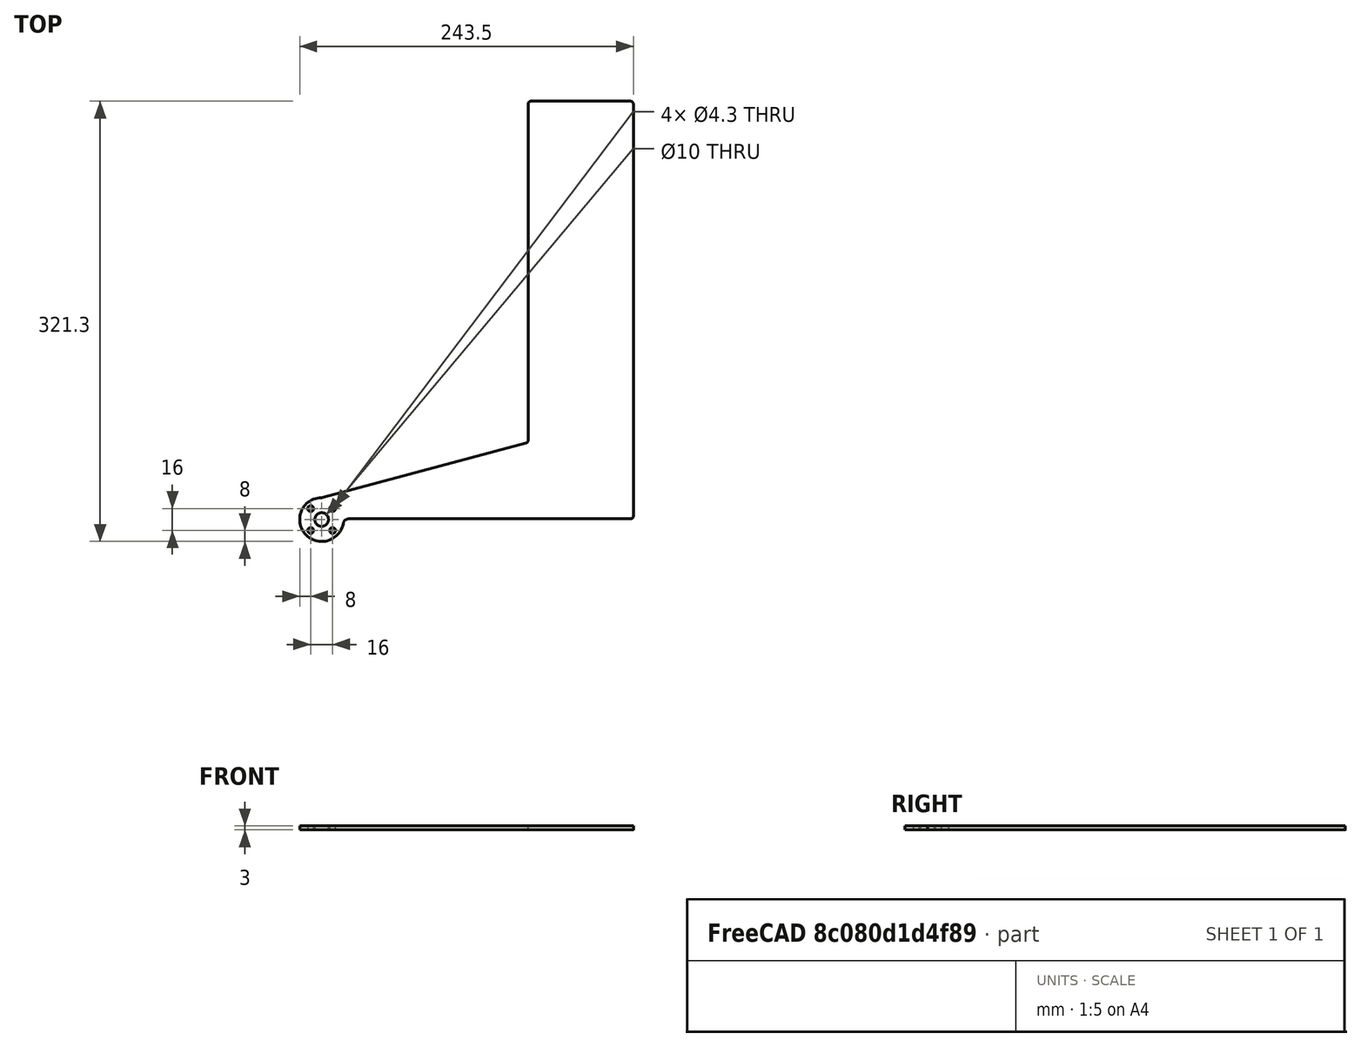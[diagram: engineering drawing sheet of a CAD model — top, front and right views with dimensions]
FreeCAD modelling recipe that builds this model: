
FCSTD DOCUMENT  (FreeCAD 0.20R29603 (Git))
Label: sleep_box_door
License: All rights reserved
LicenseURL: http://en.wikipedia.org/wiki/All_rights_reserved
objects: Sketcher::SketchObject×1, Spreadsheet::Sheet×1, PartDesign::Pad×1, PartDesign::Body×1, Part::Part2DObjectPython×1
note: 5 computed .brp shape members not serialized (recipe doc carries the construction recipe); baked Part::Feature solids carry a one-line shape summary decoded from their .brp

FEATURE [Sketcher::SketchObject] Sketch  label="DoorSketch"
  FullyConstrained = true
  MapMode = 5
  Support = -> [XY_Plane]
  expr: Constraints[11] = Spreadsheet.DoorFilletRadius
  expr: Constraints[1] = Spreadsheet.DoorHubDiameter
  expr: Constraints[25] = Spreadsheet.DoorToMazeFloorMargin
  expr: Constraints[30] = Spreadsheet.DoorHubFilletRadius
  expr: Constraints[35] = Spreadsheet.ServoSplineToMazeFloorDistance
  expr: Constraints[3] = Spreadsheet.DoorBottomLength
  expr: Constraints[53] = Spreadsheet.ServoHubMountThruHoleDiameter
  expr: Constraints[54] = Spreadsheet.ServoHubMountHoleSpacing
  expr: Constraints[56] = Spreadsheet.ServoHubCenterHoleDiameter
  expr: Constraints[5] = Spreadsheet.DoorHeight
  expr: Constraints[69] = Spreadsheet.DoorTopLength
  expr: Constraints[72] = Spreadsheet.DoorFilletRadius
  expr: Constraints[76] = Spreadsheet.DoorArmAngle
  sketch-geometry (32):
    g0: Circle CenterX=0 CenterY=0 CenterZ=0 NormalX=0 NormalY=0 NormalZ=1 AngleXU=0 Radius=16
    g1: LineSegment StartX=36.7 StartY=0.5 StartZ=0 EndX=225.5 EndY=0.5 EndZ=0
    g2: LineSegment StartX=227.5 StartY=2.5 StartZ=0 EndX=227.5 EndY=303.3 EndZ=0
    g3: LineSegment StartX=225.5 StartY=305.3 StartZ=0 EndX=152.7 EndY=305.3 EndZ=0
    g4: ArcOfCircle CenterX=225.5 CenterY=2.5 CenterZ=0 NormalX=0 NormalY=0 NormalZ=1 AngleXU=0 Radius=2 StartAngle=4.71239 EndAngle=6.28319
    g5: GeomPoint X=227.5 Y=0.5 Z=0
    g6: ArcOfCircle CenterX=225.5 CenterY=303.3 CenterZ=0 NormalX=0 NormalY=0 NormalZ=1 AngleXU=0 Radius=2 StartAngle=-1.8e-15 EndAngle=1.5708
    g7: GeomPoint X=227.5 Y=305.3 Z=0
    g8: LineSegment StartX=152.7 StartY=305.3 StartZ=0 EndX=36.7 EndY=0.5 EndZ=0
    g9: ArcOfCircle CenterX=152.7 CenterY=303.3 CenterZ=0 NormalX=0 NormalY=0 NormalZ=1 AngleXU=0 Radius=2 StartAngle=1.5708 EndAngle=3.14159
    g10: GeomPoint X=152.7 Y=305.3 Z=0
    g11: ArcOfCircle CenterX=0 CenterY=0 CenterZ=0 NormalX=0 NormalY=0 NormalZ=1 AngleXU=0 Radius=16 StartAngle=1.5708 EndAngle=6.10728
    g12: LineSegment StartX=36.7 StartY=0 StartZ=0 EndX=36.7 EndY=0.5 EndZ=0
    g13: LineSegment StartX=36.7 StartY=0.5 StartZ=0 EndX=19.6914 EndY=0.5 EndZ=0
    g14: ArcOfCircle CenterX=19.6914 CenterY=-3.5 CenterZ=0 NormalX=0 NormalY=0 NormalZ=1 AngleXU=0 Radius=4 StartAngle=1.5708 EndAngle=2.96569
    g15: ArcOfCircle CenterX=5e-16 CenterY=20 CenterZ=0 NormalX=0 NormalY=0 NormalZ=1 AngleXU=0 Radius=4 StartAngle=4.71239 EndAngle=4.97419
    g16: LineSegment StartX=-8 StartY=8 StartZ=0 EndX=8 EndY=8 EndZ=0
    g17: LineSegment StartX=8 StartY=8 StartZ=0 EndX=8 EndY=-8 EndZ=0
    g18: LineSegment StartX=8 StartY=-8 StartZ=0 EndX=-8 EndY=-8 EndZ=0
    g19: LineSegment StartX=-8 StartY=-8 StartZ=0 EndX=-8 EndY=8 EndZ=0
    g20: Circle CenterX=-8 CenterY=8 CenterZ=0 NormalX=0 NormalY=0 NormalZ=1 AngleXU=0 Radius=2.15
    g21: Circle CenterX=8 CenterY=8 CenterZ=0 NormalX=0 NormalY=0 NormalZ=1 AngleXU=0 Radius=2.15
    g22: Circle CenterX=-8 CenterY=-8 CenterZ=0 NormalX=0 NormalY=0 NormalZ=1 AngleXU=0 Radius=2.15
    g23: Circle CenterX=8 CenterY=-8 CenterZ=0 NormalX=0 NormalY=0 NormalZ=1 AngleXU=0 Radius=2.15
    g24: Circle CenterX=0 CenterY=0 CenterZ=0 NormalX=0 NormalY=0 NormalZ=1 AngleXU=0 Radius=5
    g25: LineSegment StartX=152.7 StartY=305.3 StartZ=0 EndX=152.7 EndY=0.5 EndZ=0
    g26: LineSegment StartX=36.7 StartY=0.5 StartZ=0 EndX=36.7 EndY=305.3 EndZ=0
    g27: LineSegment StartX=36.7 StartY=305.3 StartZ=0 EndX=152.7 EndY=305.3 EndZ=0
    g28: LineSegment StartX=1.03528 StartY=16.1363 StartZ=0 EndX=149.218 EndY=55.8416 EndZ=0
    g29: LineSegment StartX=150.7 StartY=303.3 StartZ=0 EndX=150.7 EndY=57.7735 EndZ=0
    g30: ArcOfCircle CenterX=148.7 CenterY=57.7735 CenterZ=0 NormalX=0 NormalY=0 NormalZ=1 AngleXU=0 Radius=2 StartAngle=4.97419 EndAngle=6.28319
    g31: LineSegment StartX=-2e-16 StartY=16 StartZ=0 EndX=152.7 EndY=16 EndZ=0
  constraints (77):
    c: Coincident(g0,g-1)
    c: Diameter(g0) = 32
    c: Horizontal(g1)
    c: DistanceX(g1,g5) = 190.8
    c: Vertical(g2)
    c: DistanceY(g5,g7) = 304.8
    c: Horizontal(g3)
    c: PointOnObject(g5,g1)
    c: PointOnObject(g5,g2)
    c: Tangent(g1,g4) = -1.5708
    c: Tangent(g2,g4) = -1.5708
    c: Radius(g4) = 2
    c: PointOnObject(g7,g3)
    c: PointOnObject(g7,g2)
    c: Tangent(g3,g6) = -1.5708
    c: Tangent(g2,g6) = -1.5708
    c: Equal(g4,g6)
    c: Coincident(g8,g10)
    c: Tangent(g3,g9) = -1.5708
    c: Equal(g6,g9)
    c: Coincident(g11,g0)
    c: PointOnObject(g11,g0)
    c: PointOnObject(g12,g-1)
    c: Vertical(g12)
    c: Coincident(g12,g1)
    c: DistanceY(g12,g12) = 0.5
    c: Coincident(g13,g1)
    c: Horizontal(g13)
    c: Tangent(g14,g13) = -1.5708
    c: Tangent(g14,g11) = 1.5708
    c: Radius(g14) = 4
    c: Tangent(g11,g15) = 1.5708
    c: Equal(g15,g14)
    c: PointOnObject(g11,g-2)
    c: Coincident(g8,g1)
    c: DistanceX(g11,g1) = 36.7
    c: Coincident(g16,g17)
    c: Coincident(g17,g18)
    c: Coincident(g18,g19)
    c: Coincident(g19,g16)
    c: Horizontal(g16)
    c: Horizontal(g18)
    c: Vertical(g17)
    c: Vertical(g19)
    c: Symmetric(g16,g17,g11)
    c: Equal(g19,g16)
    c: Coincident(g20,g16)
    c: Coincident(g21,g16)
    c: Coincident(g22,g18)
    c: Coincident(g23,g17)
    c: Equal(g20,g21)
    c: Equal(g21,g23)
    c: Equal(g23,g22)
    c: Diameter(g20) = 4.3
    c: DistanceX(g16,g16) = 16
    c: Coincident(g24,g11)
    c: Diameter(g24) = 10
    c: Coincident(g25,g8)
    c: Vertical(g25)
    c: PointOnObject(g25,g1)
    c: Coincident(g26,g1)
    c: Vertical(g26)
    c: Coincident(g27,g26)
    c: Horizontal(g27)
    c: Coincident(g8,g27)
    c: Tangent(g28,g15) = -1.5708
    c: Vertical(g29)
    c: Tangent(g29,g9) = -1.5708
    c: Coincident(g3,g8)
    c: DistanceX(g9,g7) = 76.8
    c: Tangent(g28,g30) = -1.5708
    c: Tangent(g29,g30) = 1.5708
    c: Radius(g30) = 2
    c: Coincident(g31,g11)
    c: Horizontal(g31)
    c: PointOnObject(g31,g25)
    c: Angle(g31,g28) = 0.261799
FEATURE [Spreadsheet::Sheet] Spreadsheet
  cells = A2=Servo Hub Parameters; A3=ServoHubDiameter; B3(ServoHubDiameter)==32mm; A4=ServoHubMountHoleSpacing; B4(ServoHubMountHoleSpacing)==16mm; A5=ServoHubMountThruHoleDiameter; B5(ServoHubMountThruHoleDiameter)==4.3mm; A6=ServoHubCenterHoleDiameter; B6(ServoHubCenterHoleDiameter)==10mm; A7=ServoSplineToServoMountHoleDistance; B7(ServoSplineToServoMountHoleDistance)==14.2mm; A8=ServoMountHoleToBracketBndryDistance; B8(ServoMountHoleToBracketBndryDistance)==3.5mm; A9=ServoMarginToMountPlate; B9(ServoMarginToMountPlate)==10mm; A10=MountPlateThickness; B10(MountPlateThickness)==9mm; A11=MountBeamToGapFarSide; B11(MountBeamToGapFarSide)==180.8mm; A12=MountBeamToGapNearSide; B12(MountBeamToGapNearSide)==124mm; A15=Design Parameters; A16=DoorHubDiameter; B16(DoorHubDiameter)==ServoHubDiameter; A17=DoorToMazeFloorMargin; B17(DoorToMazeFloorMargin)==0.5mm; A18=DoorOverlap; B18(DoorOverlap)==10mm; A19=ServoSplineToMazeFloorDistance; B19(ServoSplineToMazeFloorDistance)==ServoSplineToServoMountHoleDistance + ServoMountHoleToBracketBndryDistance + ServoMarginToMountPlate + MountPlateThickness; A20=DoorBottomLength; B20(DoorBottomLength)==MountBeamToGapFarSide + DoorOverlap; A21=DoorTopLength; B21(DoorTopLength)==DoorBottomLength - (MountBeamToGapNearSide - DoorOverlap); A22=DoorHeight; B22(DoorHeight)==12in; A23=DoorFilletRadius; B23(DoorFilletRadius)==2mm; A24=DoorHubFilletRadius; B24(DoorHubFilletRadius)==4mm; A25=DoorThickness; B25(DoorThickness)==3mm; A26=DoorArmAngle; B26(DoorArmAngle)==15deg
FEATURE [PartDesign::Pad] Pad
  Direction = (0,0,1)
  Length = 3
  Length2 = 10
  Profile = -> Sketch
  ReferenceAxis = -> Sketch [N_Axis]
  Type = 0
  expr: Length = Spreadsheet.DoorThickness
FEATURE [PartDesign::Body] Body
  Group = -> [Sketch,Pad]
  Origin = -> Origin
  Tip = -> Pad
FEATURE [Part::Part2DObjectPython] Shape2DView  # Draft 2D object (typed FeaturePython)
  AutoUpdate = true
  Base = -> Pad
  Clip = false
  FaceNumbers = [17]
  FuseArch = false
  HiddenLines = false
  InPlace = true
  OnlySolids = false
  Projection = (0,0,1)
  ProjectionMode = 0
  SegmentLength = 0.05
  Tessellation = false
  VisibleOnly = false
